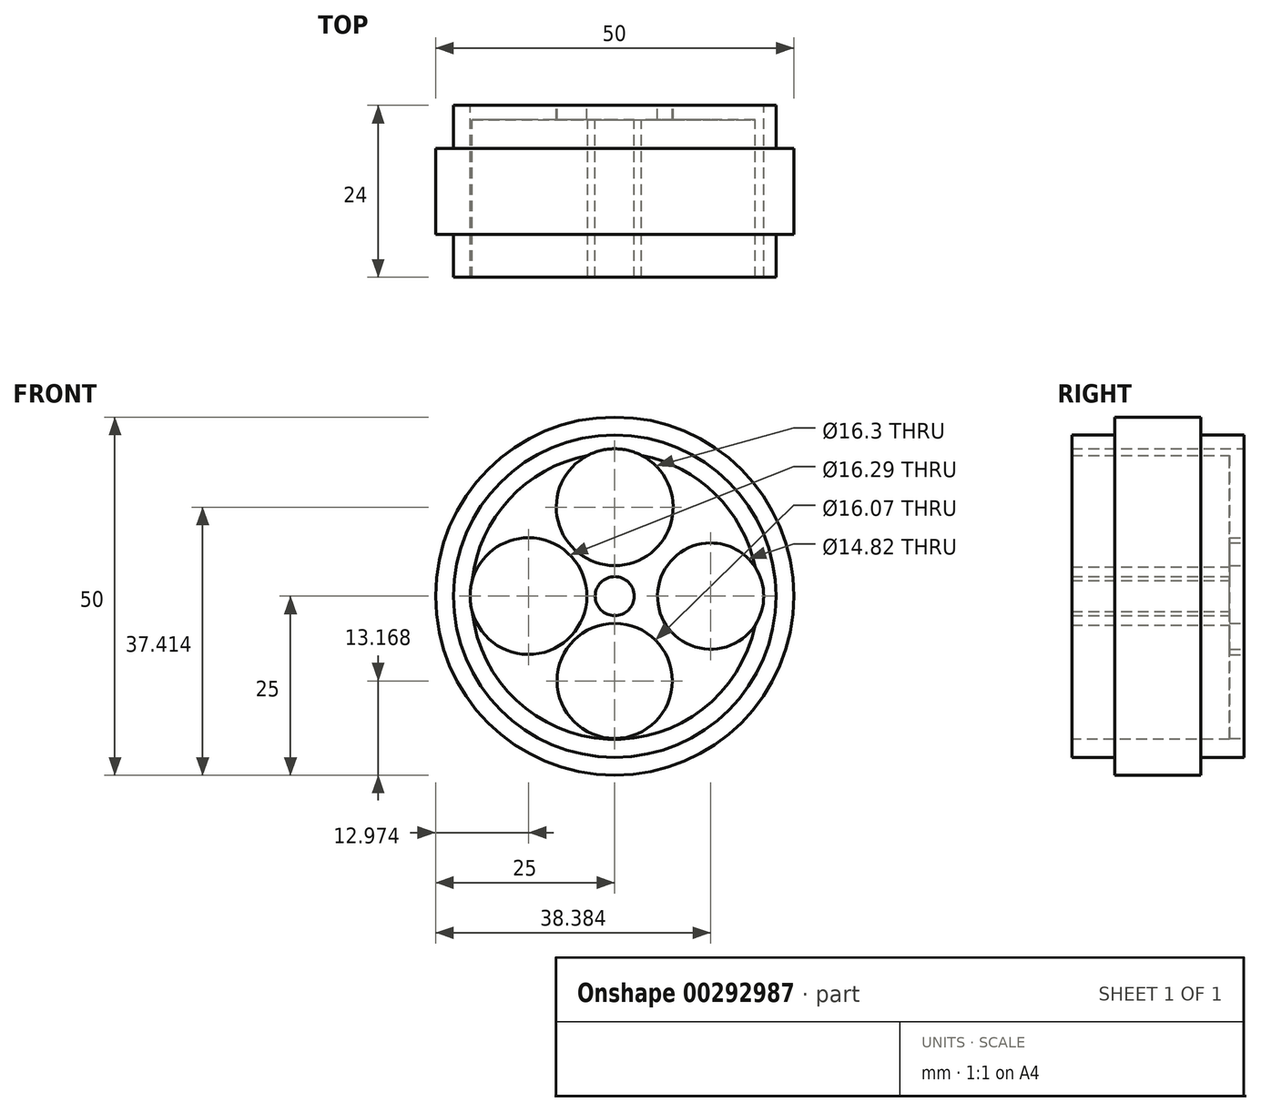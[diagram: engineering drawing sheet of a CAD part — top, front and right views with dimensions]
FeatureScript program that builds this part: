
annotation { "Feature Type Name" : "Feature", "Feature Type Description" : "" }
export const myFeature = defineFeature(function(context is Context, id is Id, definition is map)
    precondition{}
    {
        {
            var Q0;
            Q0=qCreatedBy(makeId("Front.planeOp"),FACE);
            var sketch = newSketch(context, id + "F0", { "sketchPlane" : qUnion([Q0])});
            skCircle(sketch, "E0", {"center": v(0, 0) * mm, "radius": 22.5 * mm});
            skSolve(sketch);
        }
        {
            var Q0;
            Q0=makeQuery(id+"F0.imprint","IMPRINT",FACE,{"disambiguationData":[TD([[makeQuery(id+"F0.imprint","IMPRINT",EDGE,{"derivedFrom":sQuery(id+"F0.wireOp",EDGE,"E0")}),1.0]])]});
            extrude(context, id + "F1", {"entities" : qUnion([Q0]), "depth" : 6 * mm});
        }
        {
            var Q0;
            Q0=makeQuery(id+"F1.opExtrude","CAP_FACE",FACE,{"disambiguationData":[OSD([sQuery(id+"F0.wireOp",EDGE,"E0")])],"isStart":false});
            var sketch = newSketch(context, id + "F2", { "sketchPlane" : qUnion([Q0])});
            skCircle(sketch, "E1", {"center": v(0, 0) * mm, "radius": 25 * mm});
            skSolve(sketch);
        }
        {
            var Q0;
            Q0=makeQuery(id+"F2.imprint","IMPRINT",FACE,{"disambiguationData":[TD([[makeQuery(id+"F2.imprint","IMPRINT",EDGE,{"derivedFrom":makeQuery(id+"F1.opExtrude","CAP_EDGE",EDGE,{"disambiguationData":[OSD([sQuery(id+"F0.wireOp",EDGE,"E0")])],"isStart":false})}),1.0]])]});
            var Q1;
            Q1=makeQuery(id+"F2.imprint","IMPRINT",FACE,{"disambiguationData":[TD([[makeQuery(id+"F2.imprint","IMPRINT",EDGE,{"derivedFrom":sQuery(id+"F2.wireOp",EDGE,"E1")}),1.0]])]});
            extrude(context, id + "F3", {"entities" : qUnion([Q0, Q1]), "operationType" : NewBodyOperationType.ADD, "depth" : 12 * mm});
        }
        {
            var Q0;
            Q0=makeQuery(id+"F3.opExtrude","CAP_FACE",FACE,{"disambiguationData":[OSD([sQuery(id+"F2.wireOp",EDGE,"E1")])],"isStart":false});
            var sketch = newSketch(context, id + "F4", { "sketchPlane" : qUnion([Q0])});
            skCircle(sketch, "E2", {"center": v(0, 0) * mm, "radius": 22.5 * mm});
            skSolve(sketch);
        }
        {
            var Q0;
            Q0=makeQuery(id+"F4.imprint","IMPRINT",FACE,{"disambiguationData":[TD([[makeQuery(id+"F4.imprint","IMPRINT",EDGE,{"derivedFrom":sQuery(id+"F4.wireOp",EDGE,"E2")}),1.0]])]});
            extrude(context, id + "F5", {"entities" : qUnion([Q0]), "operationType" : NewBodyOperationType.ADD, "depth" : 6 * mm});
        }
        {
            var Q0;
            Q0=makeQuery(id+"F5.opExtrude","CAP_FACE",FACE,{"disambiguationData":[OSD([sQuery(id+"F4.wireOp",EDGE,"E2")])],"isStart":false});
            var sketch = newSketch(context, id + "F6", { "sketchPlane" : qUnion([Q0])});
            skCircle(sketch, "E3", {"center": v(0, 0) * mm, "radius": 20 * mm});
            skSolve(sketch);
        }
        {
            var Q0;
            Q0=makeQuery(id+"F6.imprint","IMPRINT",FACE,{"disambiguationData":[TD([[makeQuery(id+"F6.imprint","IMPRINT",EDGE,{"derivedFrom":sQuery(id+"F6.wireOp",EDGE,"E3")}),1.0]])]});
            extrude(context, id + "F7", {"entities" : qUnion([Q0]), "operationType" : NewBodyOperationType.REMOVE, "oppositeDirection" : true, "depth" : 22 * mm});
        }
        {
            var Q0;
            Q0=makeQuery(id+"F1.opExtrude","CAP_FACE",FACE,{"disambiguationData":[OSD([sQuery(id+"F0.wireOp",EDGE,"E0")])],"isStart":true});
            var sketch = newSketch(context, id + "F8", { "sketchPlane" : qUnion([Q0])});
            skCircle(sketch, "E4", {"center": v(0, 12.41) * mm, "radius": 8.15 * mm});
            skSolve(sketch);
        }
        {
            var Q0;
            Q0=makeQuery(id+"F8.imprint","IMPRINT",FACE,{"disambiguationData":[TD([[makeQuery(id+"F8.imprint","IMPRINT",EDGE,{"derivedFrom":sQuery(id+"F8.wireOp",EDGE,"E4")}),1.0]])]});
            extrude(context, id + "F9", {"entities" : qUnion([Q0]), "operationType" : NewBodyOperationType.REMOVE, "oppositeDirection" : true, "depth" : 25 * mm});
        }
        {
            var Q0;
            Q0=makeQuery(id+"F1.opExtrude","CAP_FACE",FACE,{"disambiguationData":[OSD([sQuery(id+"F0.wireOp",EDGE,"E0")])],"isStart":true});
            var sketch = newSketch(context, id + "F10", { "sketchPlane" : qUnion([Q0])});
            skCircle(sketch, "E5", {"center": v(12.03, 0) * mm, "radius": 8.15 * mm});
            skSolve(sketch);
        }
        {
            var Q0;
            Q0=makeQuery(id+"F10.imprint","IMPRINT",FACE,{"disambiguationData":[TD([[makeQuery(id+"F10.imprint","IMPRINT",EDGE,{"derivedFrom":sQuery(id+"F10.wireOp",EDGE,"E5")}),1.0]])]});
            extrude(context, id + "F11", {"entities" : qUnion([Q0]), "operationType" : NewBodyOperationType.REMOVE, "oppositeDirection" : true, "depth" : 25 * mm});
        }
        {
            var Q0;
            Q0=makeQuery(id+"F1.opExtrude","CAP_FACE",FACE,{"disambiguationData":[OSD([sQuery(id+"F0.wireOp",EDGE,"E0")])],"isStart":true});
            var sketch = newSketch(context, id + "F12", { "sketchPlane" : qUnion([Q0])});
            skCircle(sketch, "E6", {"center": v(0, -11.83) * mm, "radius": 8.04 * mm});
            skSolve(sketch);
        }
        {
            var Q0;
            Q0=makeQuery(id+"F12.imprint","IMPRINT",FACE,{"disambiguationData":[TD([[makeQuery(id+"F12.imprint","IMPRINT",EDGE,{"derivedFrom":sQuery(id+"F12.wireOp",EDGE,"E6")}),1.0]])]});
            extrude(context, id + "F13", {"entities" : qUnion([Q0]), "operationType" : NewBodyOperationType.REMOVE, "oppositeDirection" : true, "depth" : 25 * mm});
        }
        {
            var Q0;
            Q0=makeQuery(id+"F1.opExtrude","CAP_FACE",FACE,{"disambiguationData":[OSD([sQuery(id+"F0.wireOp",EDGE,"E0")])],"isStart":true});
            var sketch = newSketch(context, id + "F14", { "sketchPlane" : qUnion([Q0])});
            skCircle(sketch, "E7", {"center": v(-13.38, 0) * mm, "radius": 7.41 * mm});
            skSolve(sketch);
        }
        {
            var Q0;
            Q0=makeQuery(id+"F14.imprint","IMPRINT",FACE,{"disambiguationData":[TD([[makeQuery(id+"F14.imprint","IMPRINT",EDGE,{"derivedFrom":sQuery(id+"F14.wireOp",EDGE,"E7")}),1.0]])]});
            extrude(context, id + "F15", {"entities" : qUnion([Q0]), "operationType" : NewBodyOperationType.REMOVE, "oppositeDirection" : true, "depth" : 25 * mm});
        }
        {
            var Q0;
            Q0=makeQuery(id+"F7.boolean.opBoolean","COPY",FACE,{"derivedFrom":makeQuery(id+"F7.opExtrude","CAP_FACE",FACE,{"disambiguationData":[OSD([sQuery(id+"F6.wireOp",EDGE,"E3")])],"isStart":false})});
            var sketch = newSketch(context, id + "F16", { "sketchPlane" : qUnion([Q0])});
            skCircle(sketch, "E8", {"center": v(0, 0) * mm, "radius": 2.72 * mm});
            skSolve(sketch);
        }
        {
            var Q0;
            Q0=makeQuery(id+"F16.imprint","IMPRINT",FACE,{"disambiguationData":[TD([[makeQuery(id+"F16.imprint","IMPRINT",EDGE,{"derivedFrom":sQuery(id+"F16.wireOp",EDGE,"E8")}),1.0]])]});
            extrude(context, id + "F17", {"entities" : qUnion([Q0]), "operationType" : NewBodyOperationType.ADD, "depth" : 22 * mm});
        }
    });
